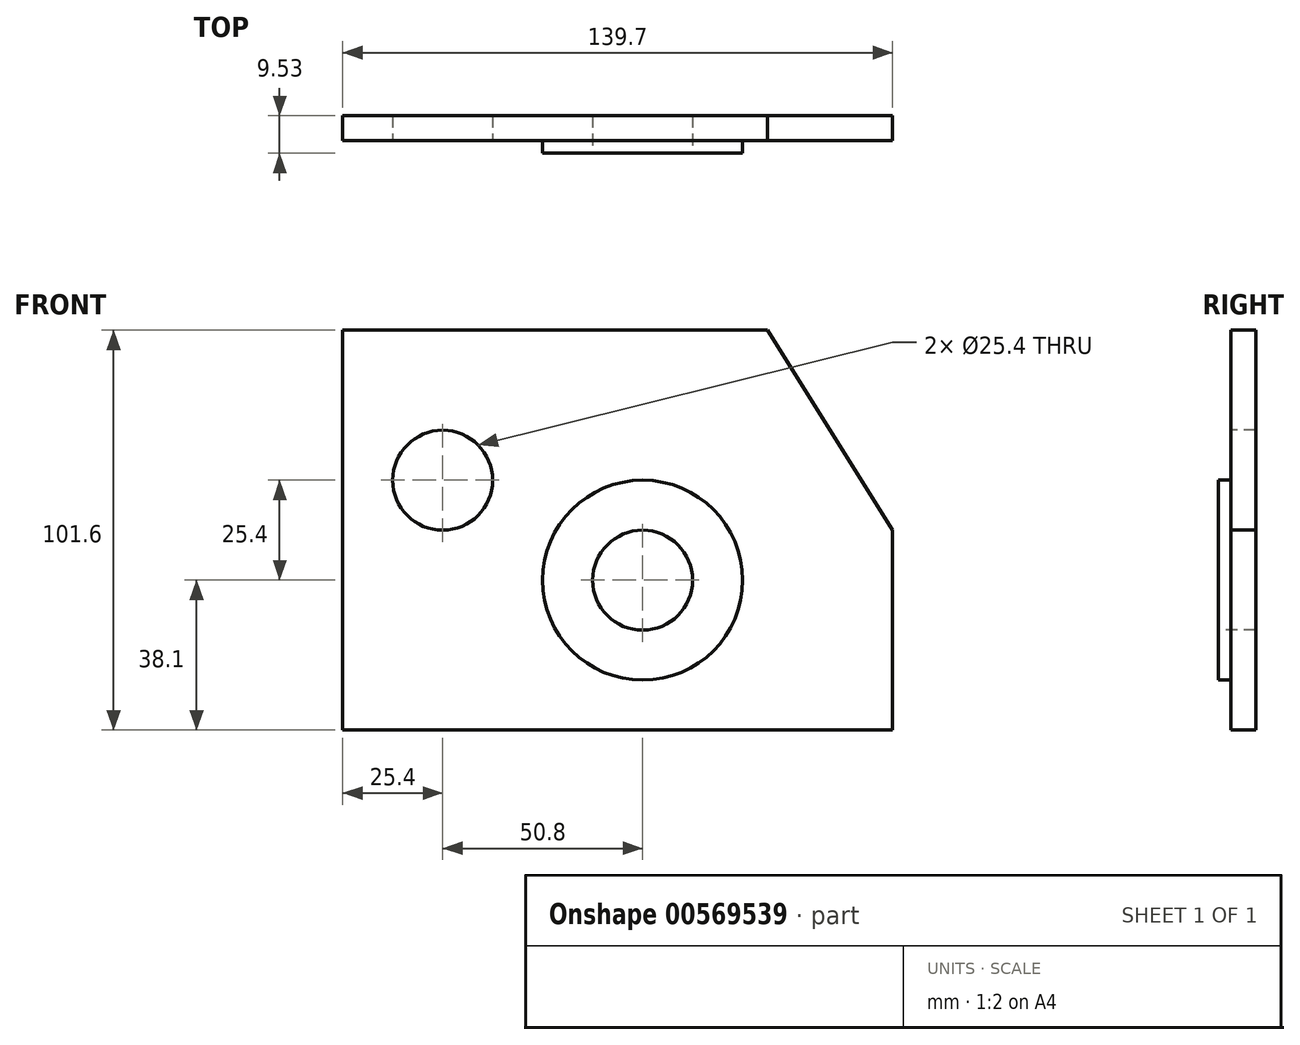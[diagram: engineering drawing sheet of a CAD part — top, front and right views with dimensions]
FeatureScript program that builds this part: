
annotation { "Feature Type Name" : "Feature", "Feature Type Description" : "" }
export const myFeature = defineFeature(function(context is Context, id is Id, definition is map)
    precondition{}
    {
        {
            var Q0;
            Q0=qCreatedBy(makeId("Front.planeOp"),FACE);
            var sketch = newSketch(context, id + "F0", { "sketchPlane" : qUnion([Q0])});
            skLineSegment(sketch, "E0.bottom", {"start": v(0, 0) * mm, "end": v(139.7, 0) * mm});
            skLineSegment(sketch, "E0.top", {"start": v(0, 101.6) * mm, "end": v(107.95, 101.6) * mm});
            skLineSegment(sketch, "E0.left", {"start": v(0, 0) * mm, "end": v(0, 101.6) * mm});
            skLineSegment(sketch, "E0.right", {"start": v(139.7, 0) * mm, "end": v(139.7, 50.8) * mm});
            skLineSegment(sketch, "E1.bottom", {"start": v(0, 0) * mm, "end": v(76.2, 0) * mm});
            skLineSegment(sketch, "E1.left", {"start": v(0, 0) * mm, "end": v(0, 38.1) * mm});
            skCircle(sketch, "E2", {"center": v(76.2, 38.1) * mm, "radius": 12.7 * mm});
            skCircle(sketch, "E3", {"center": v(76.2, 38.1) * mm, "radius": 25.4 * mm});
            skLineSegment(sketch, "E4.bottom", {"start": v(0, 0) * mm, "end": v(25.4, 0) * mm});
            skLineSegment(sketch, "E4.left", {"start": v(0, 0) * mm, "end": v(0, 63.5) * mm});
            skCircle(sketch, "E5", {"center": v(25.4, 63.5) * mm, "radius": 12.7 * mm});
            skLineSegment(sketch, "E6", {"start": v(107.95, 101.6) * mm, "end": v(139.7, 50.8) * mm});
            skSolve(sketch);
        }
        {
            var Q0;
            Q0=makeQuery(id+"F0.imprint","IMPRINT",FACE,{"disambiguationData":[TD([[makeQuery(id+"F0.imprint","IMPRINT",EDGE,{"derivedFrom":sQuery(id+"F0.wireOp",EDGE,"E0.bottom")}),1.0]])]});
            var Q1;
            Q1=makeQuery(id+"F0.imprint","IMPRINT",FACE,{"disambiguationData":[TD([[makeQuery(id+"F0.imprint","IMPRINT",EDGE,{"derivedFrom":sQuery(id+"F0.wireOp",EDGE,"E2")}),-1.0]])]});
            extrude(context, id + "F1", {"entities" : qUnion([Q0, Q1]), "oppositeDirection" : true, "depth" : 6.35 * mm, "offsetDistance" : 25.4 * mm});
        }
        {
            var Q0;
            Q0=makeQuery(id+"F0.imprint","IMPRINT",FACE,{"disambiguationData":[TD([[makeQuery(id+"F0.imprint","IMPRINT",EDGE,{"derivedFrom":sQuery(id+"F0.wireOp",EDGE,"E2")}),-1.0]])]});
            extrude(context, id + "F2", {"entities" : qUnion([Q0]), "operationType" : NewBodyOperationType.ADD, "depth" : 3.17 * mm, "offsetDistance" : 25.4 * mm});
        }
    });
